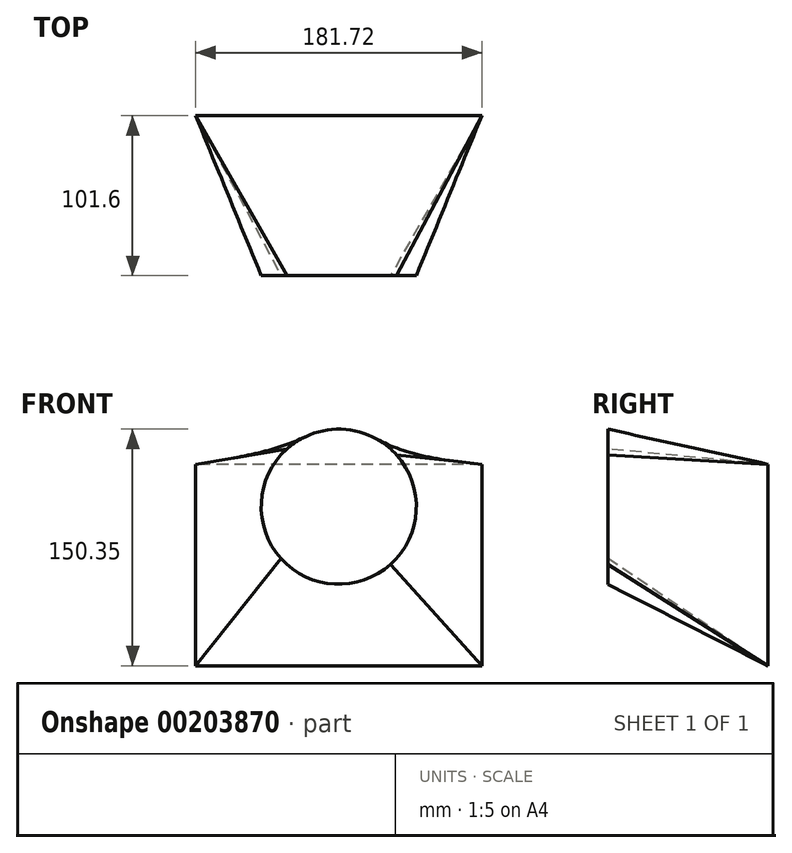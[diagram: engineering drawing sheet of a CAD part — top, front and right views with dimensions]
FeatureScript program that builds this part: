
annotation { "Feature Type Name" : "Feature", "Feature Type Description" : "" }
export const myFeature = defineFeature(function(context is Context, id is Id, definition is map)
    precondition{}
    {
        {
            var Q0;
            Q0=qCreatedBy(makeId("Front.planeOp"),FACE);
            var sketch = newSketch(context, id + "F0", { "sketchPlane" : qUnion([Q0])});
            skLineSegment(sketch, "E0.bottom", {"start": v(90.86, -64.03) * mm, "end": v(-90.86, -64.03) * mm});
            skLineSegment(sketch, "E0.top", {"start": v(90.86, 64.03) * mm, "end": v(-90.86, 64.03) * mm});
            skLineSegment(sketch, "E0.left", {"start": v(90.86, -64.03) * mm, "end": v(90.86, 64.03) * mm});
            skLineSegment(sketch, "E0.right", {"start": v(-90.86, -64.03) * mm, "end": v(-90.86, 64.03) * mm});
            skPoint(sketch, "E0.middle", {"position": v(0, 0) * mm});
            skSolve(sketch);
        }
        {
            var Q0;
            Q0=qCreatedBy(makeId("Front.planeOp"),FACE);
            cPlane(context, id + "F1", {"entities" : qUnion([Q0]), "cplaneType" : CPlaneType.OFFSET, "offset" : 101.6 * mm, "width" : 152.4 * mm, "height" : 152.4 * mm});
        }
        {
            var Q0;
            Q0=qCreatedBy(id+"F1.planeOp",FACE);
            var sketch = newSketch(context, id + "F2", { "sketchPlane" : qUnion([Q0])});
            skCircle(sketch, "E1", {"center": v(0, 37.05) * mm, "radius": 49.27 * mm});
            skSolve(sketch);
        }
        {
            var Q0;
            Q0=makeQuery(id+"F0.imprint","IMPRINT",FACE,{"disambiguationData":[TD([[makeQuery(id+"F0.imprint","IMPRINT",EDGE,{"derivedFrom":sQuery(id+"F0.wireOp",EDGE,"E0.bottom")}),-1.0]])]});
            var Q1;
            Q1=makeQuery(id+"F2.imprint","IMPRINT",FACE,{"disambiguationData":[TD([[makeQuery(id+"F2.imprint","IMPRINT",EDGE,{"derivedFrom":sQuery(id+"F2.wireOp",EDGE,"E1")}),1.0]])]});
            loft(context, id + "F3", {"sheetProfilesArray" : [{ "sheetProfileEntities" : qUnion([Q0]) }, { "sheetProfileEntities" : qUnion([Q1]) }]});
        }
    });
